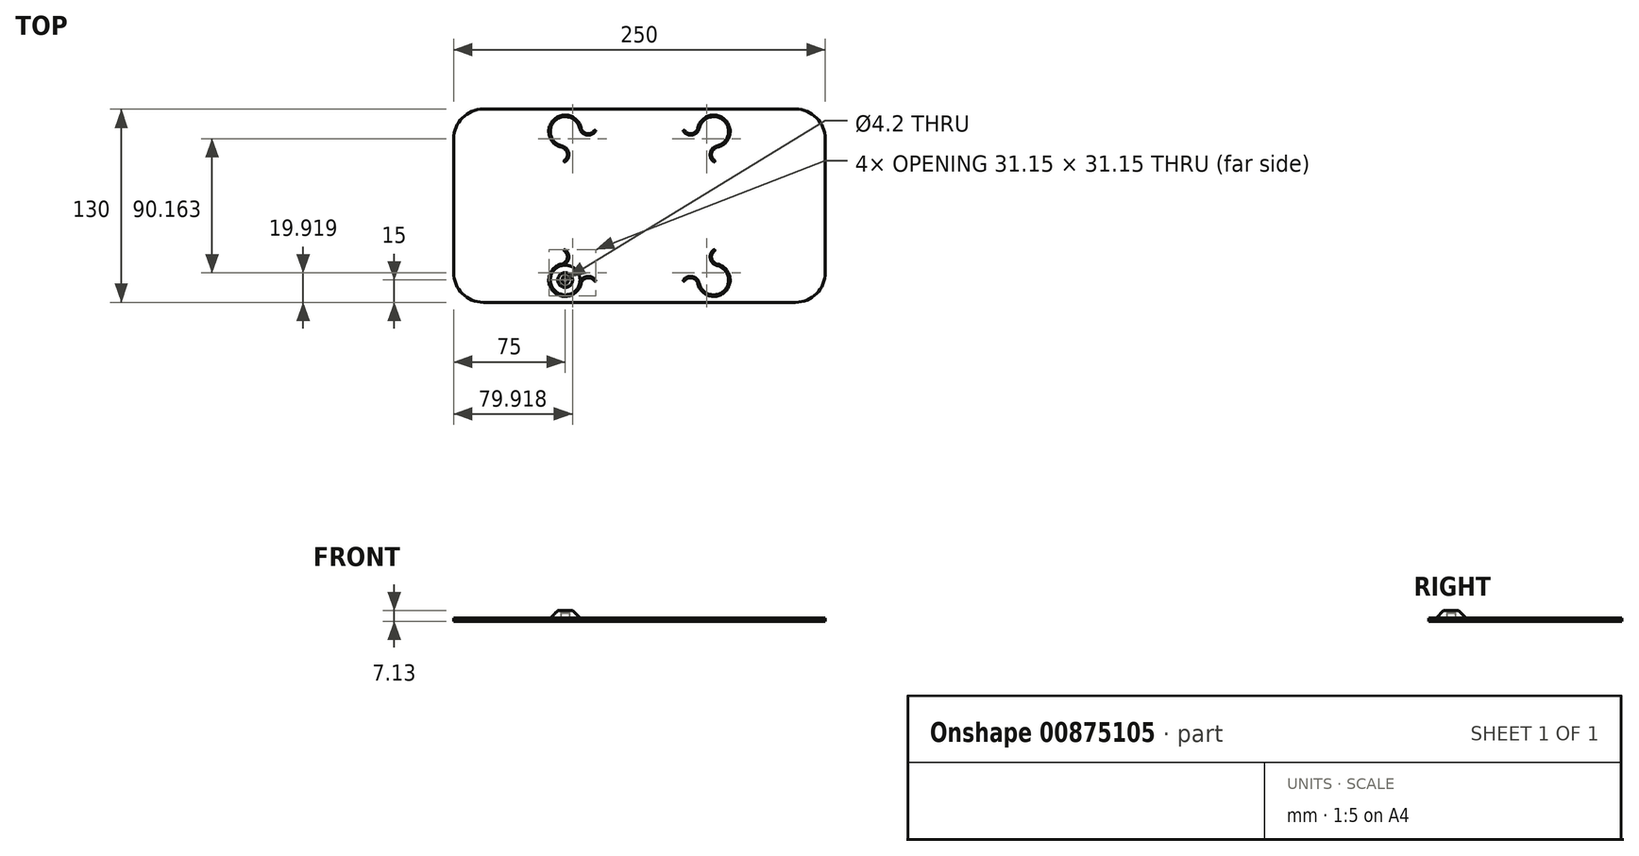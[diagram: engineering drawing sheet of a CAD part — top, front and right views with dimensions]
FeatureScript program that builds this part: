
annotation { "Feature Type Name" : "Feature", "Feature Type Description" : "" }
export const myFeature = defineFeature(function(context is Context, id is Id, definition is map)
    precondition{}
    {
        {
            var Q0;
            Q0=qCreatedBy(makeId("Top.planeOp"),FACE);
            var sketch = newSketch(context, id + "F0", { "sketchPlane" : qUnion([Q0])});
            skLineSegment(sketch, "E0.bottom", {"start": v(-105, 65) * mm, "end": v(105, 65) * mm});
            skLineSegment(sketch, "E0.top", {"start": v(-105, -65) * mm, "end": v(105, -65) * mm});
            skLineSegment(sketch, "E0.left", {"start": v(-125, 45) * mm, "end": v(-125, -45) * mm});
            skLineSegment(sketch, "E0.right", {"start": v(125, 45) * mm, "end": v(125, -45) * mm});
            skPoint(sketch, "E0.middle", {"position": v(0, 0) * mm});
            skLineSegment(sketch, "E1.bottom", {"start": v(50, -50) * mm, "end": v(-50, -50) * mm, "construction": true});
            skLineSegment(sketch, "E1.top", {"start": v(50, 50) * mm, "end": v(-50, 50) * mm, "construction": true});
            skLineSegment(sketch, "E1.left", {"start": v(50, -50) * mm, "end": v(50, 50) * mm, "construction": true});
            skLineSegment(sketch, "E1.right", {"start": v(-50, -50) * mm, "end": v(-50, 50) * mm, "construction": true});
            skArc(sketch, "E2", {"start": v(-40.24, 52.16) * mm, "mid": v(-57.07, 57.07) * mm, "end": v(-52.16, 40.24) * mm});
            skLineSegment(sketch, "E3", {"start": v(0, 0) * mm, "end": v(-50, 0) * mm, "construction": true});
            skLineSegment(sketch, "E4", {"start": v(0, 0) * mm, "end": v(0, 50) * mm, "construction": true});
            skArc(sketch, "E5", {"start": v(-50, 29.6) * mm, "mid": v(-47.62, 35.62) * mm, "end": v(-52.16, 40.24) * mm});
            skLineSegment(sketch, "E6", {"start": v(-50, 50) * mm, "end": v(0, 0) * mm, "construction": true});
            skArc(sketch, "E7.MirrorCS", {"start": v(-29.6, 50) * mm, "mid": v(-35.62, 47.62) * mm, "end": v(-40.24, 52.16) * mm});
            skArc(sketch, "E8.0", {"start": v(-50.58, 30.4) * mm, "mid": v(-48.6, 35.42) * mm, "end": v(-52.38, 39.26) * mm});
            skArc(sketch, "E8.1", {"start": v(-39.26, 52.38) * mm, "mid": v(-57.78, 57.78) * mm, "end": v(-52.38, 39.26) * mm});
            skArc(sketch, "E8.2", {"start": v(-30.4, 50.58) * mm, "mid": v(-35.42, 48.6) * mm, "end": v(-39.26, 52.38) * mm});
            skArc(sketch, "E9", {"start": v(-50.58, 30.4) * mm, "mid": v(-50.7, 29.71) * mm, "end": v(-50, 29.6) * mm});
            skArc(sketch, "E10.MirrorCS", {"start": v(-30.4, 50.58) * mm, "mid": v(-29.71, 50.7) * mm, "end": v(-29.6, 50) * mm});
            skPoint(sketch, "E11.visualSharp", {"position": v(-125, 65) * mm});
            skArc(sketch, "E11.filletArc", {"start": v(-105, 65) * mm, "mid": v(-119.14, 59.14) * mm, "end": v(-125, 45) * mm});
            skPoint(sketch, "E12.visualSharp", {"position": v(-125, -65) * mm});
            skArc(sketch, "E12.filletArc", {"start": v(-125, -45) * mm, "mid": v(-119.14, -59.14) * mm, "end": v(-105, -65) * mm});
            skPoint(sketch, "E13.visualSharp", {"position": v(125, -65) * mm});
            skArc(sketch, "E13.filletArc", {"start": v(105, -65) * mm, "mid": v(119.14, -59.14) * mm, "end": v(125, -45) * mm});
            skPoint(sketch, "E14.visualSharp", {"position": v(125, 65) * mm});
            skArc(sketch, "E14.filletArc", {"start": v(125, 45) * mm, "mid": v(119.14, 59.14) * mm, "end": v(105, 65) * mm});
            skArc(sketch, "E15.1.0", {"start": v(-52.38, -39.26) * mm, "mid": v(-57.78, -57.78) * mm, "end": v(-39.26, -52.38) * mm});
            skArc(sketch, "E15.1.1", {"start": v(-30.4, -50.58) * mm, "mid": v(-35.42, -48.6) * mm, "end": v(-39.26, -52.38) * mm});
            skArc(sketch, "E15.1.2", {"start": v(-52.16, -40.24) * mm, "mid": v(-57.07, -57.07) * mm, "end": v(-40.24, -52.16) * mm});
            skArc(sketch, "E15.1.3", {"start": v(-50, -29.6) * mm, "mid": v(-47.62, -35.62) * mm, "end": v(-52.16, -40.24) * mm});
            skArc(sketch, "E15.1.4", {"start": v(-50.58, -30.4) * mm, "mid": v(-48.6, -35.42) * mm, "end": v(-52.38, -39.26) * mm});
            skArc(sketch, "E15.1.5", {"start": v(-29.6, -50) * mm, "mid": v(-35.62, -47.62) * mm, "end": v(-40.24, -52.16) * mm});
            skArc(sketch, "E15.1.6", {"start": v(-30.4, -50.58) * mm, "mid": v(-29.71, -50.7) * mm, "end": v(-29.6, -50) * mm});
            skArc(sketch, "E15.1.7", {"start": v(-50.58, -30.4) * mm, "mid": v(-50.7, -29.71) * mm, "end": v(-50, -29.6) * mm});
            skArc(sketch, "E15.2.0", {"start": v(39.26, -52.38) * mm, "mid": v(57.78, -57.78) * mm, "end": v(52.38, -39.26) * mm});
            skArc(sketch, "E15.2.1", {"start": v(50.58, -30.4) * mm, "mid": v(48.6, -35.42) * mm, "end": v(52.38, -39.26) * mm});
            skArc(sketch, "E15.2.2", {"start": v(40.24, -52.16) * mm, "mid": v(57.07, -57.07) * mm, "end": v(52.16, -40.24) * mm});
            skArc(sketch, "E15.2.3", {"start": v(29.6, -50) * mm, "mid": v(35.62, -47.62) * mm, "end": v(40.24, -52.16) * mm});
            skArc(sketch, "E15.2.4", {"start": v(30.4, -50.58) * mm, "mid": v(35.42, -48.6) * mm, "end": v(39.26, -52.38) * mm});
            skArc(sketch, "E15.2.5", {"start": v(50, -29.6) * mm, "mid": v(47.62, -35.62) * mm, "end": v(52.16, -40.24) * mm});
            skArc(sketch, "E15.2.6", {"start": v(50.58, -30.4) * mm, "mid": v(50.7, -29.71) * mm, "end": v(50, -29.6) * mm});
            skArc(sketch, "E15.2.7", {"start": v(30.4, -50.58) * mm, "mid": v(29.71, -50.7) * mm, "end": v(29.6, -50) * mm});
            skArc(sketch, "E15.3.0", {"start": v(52.38, 39.26) * mm, "mid": v(57.78, 57.78) * mm, "end": v(39.26, 52.38) * mm});
            skArc(sketch, "E15.3.1", {"start": v(30.4, 50.58) * mm, "mid": v(35.42, 48.6) * mm, "end": v(39.26, 52.38) * mm});
            skArc(sketch, "E15.3.2", {"start": v(52.16, 40.24) * mm, "mid": v(57.07, 57.07) * mm, "end": v(40.24, 52.16) * mm});
            skArc(sketch, "E15.3.3", {"start": v(50, 29.6) * mm, "mid": v(47.62, 35.62) * mm, "end": v(52.16, 40.24) * mm});
            skArc(sketch, "E15.3.4", {"start": v(50.58, 30.4) * mm, "mid": v(48.6, 35.42) * mm, "end": v(52.38, 39.26) * mm});
            skArc(sketch, "E15.3.5", {"start": v(29.6, 50) * mm, "mid": v(35.62, 47.62) * mm, "end": v(40.24, 52.16) * mm});
            skArc(sketch, "E15.3.6", {"start": v(30.4, 50.58) * mm, "mid": v(29.71, 50.7) * mm, "end": v(29.6, 50) * mm});
            skArc(sketch, "E15.3.7", {"start": v(50.58, 30.4) * mm, "mid": v(50.7, 29.71) * mm, "end": v(50, 29.6) * mm});
            skCircle(sketch, "E16", {"center": v(0, 0) * mm, "radius": 50 * mm, "construction": true});
            skSolve(sketch);
        }
        {
            var Q0;
            Q0=qCreatedBy(makeId("Front.planeOp"),FACE);
            var Q1;
            Q1=sQuery(id+"F0.wireOp",VERTEX,"E1.bottom.end");
            cPlane(context, id + "F1", {"entities" : qUnion([Q0, Q1]), "cplaneType" : CPlaneType.PLANE_POINT, "offset" : 25 * mm, "width" : 150 * mm, "height" : 150 * mm});
        }
        {
            var Q0;
            Q0=makeQuery(id+"F0.imprint","IMPRINT",FACE,{"disambiguationData":[TD([[makeQuery(id+"F0.imprint","IMPRINT",EDGE,{"derivedFrom":sQuery(id+"F0.wireOp",EDGE,"E0.bottom")}),-1.0]])]});
            extrude(context, id + "F2", {"entities" : qUnion([Q0]), "depth" : 2 * mm, "offsetDistance" : 25 * mm});
        }
        {
            var Q0;
            Q0=qCreatedBy(id+"F1.planeOp",FACE);
            var sketch = newSketch(context, id + "F3", { "sketchPlane" : qUnion([Q0])});
            skLineSegment(sketch, "E17", {"start": v(-50, 0) * mm, "end": v(-50, 7.13) * mm});
            skLineSegment(sketch, "E18", {"start": v(-53.55, 0) * mm, "end": v(-52.97, 1) * mm});
            skLineSegment(sketch, "E19", {"start": v(-52.97, 1) * mm, "end": v(-52.85, 5.7) * mm});
            skLineSegment(sketch, "E20", {"start": v(-52.1, 7.13) * mm, "end": v(-55, 7.13) * mm});
            skLineSegment(sketch, "E21", {"start": v(-55, 7.13) * mm, "end": v(-60, 2) * mm});
            skLineSegment(sketch, "E22", {"start": v(-60, 0) * mm, "end": v(-53.55, 0) * mm});
            skLineSegment(sketch, "E23", {"start": v(-52.85, 5.7) * mm, "end": v(-52.1, 6.13) * mm});
            skLineSegment(sketch, "E24", {"start": v(-52.1, 6.13) * mm, "end": v(-52.1, 7.13) * mm});
            skLineSegment(sketch, "E25", {"start": v(-53.55, 0) * mm, "end": v(-50, 0) * mm});
            skLineSegment(sketch, "E26", {"start": v(-50, 7.13) * mm, "end": v(-52.1, 7.13) * mm});
            skLineSegment(sketch, "E27", {"start": v(-60, 2) * mm, "end": v(-60, 0) * mm});
            skSolve(sketch);
        }
        {
            var Q0;
            Q0=makeQuery(id+"F3.imprint","IMPRINT",FACE,{"disambiguationData":[TD([[makeQuery(id+"F3.imprint","IMPRINT",EDGE,{"derivedFrom":sQuery(id+"F3.wireOp",EDGE,"E18")}),1.0]])]});
            var Q1;
            Q1=sQuery(id+"F3.wireOp",EDGE,"E17");
            revolve(context, id + "F4", {"operationType" : NewBodyOperationType.ADD, "surfaceOperationType" : NewSurfaceOperationType.NEW, "entities" : qUnion([Q0]), "axis" : qUnion([Q1]), "revolveType" : RevolveType.FULL});
        }
        {
            var Q0;
            Q0=makeQuery(id+"F3.imprint","IMPRINT",FACE,{"disambiguationData":[TD([[makeQuery(id+"F3.imprint","IMPRINT",EDGE,{"derivedFrom":sQuery(id+"F3.wireOp",EDGE,"E17")}),1.0]])]});
            var Q1;
            Q1=sQuery(id+"F3.wireOp",EDGE,"E17");
            revolve(context, id + "F5", {"operationType" : NewBodyOperationType.REMOVE, "surfaceOperationType" : NewSurfaceOperationType.NEW, "entities" : qUnion([Q0]), "axis" : qUnion([Q1]), "revolveType" : RevolveType.FULL, "oppositeDirection" : true});
        }
    });
